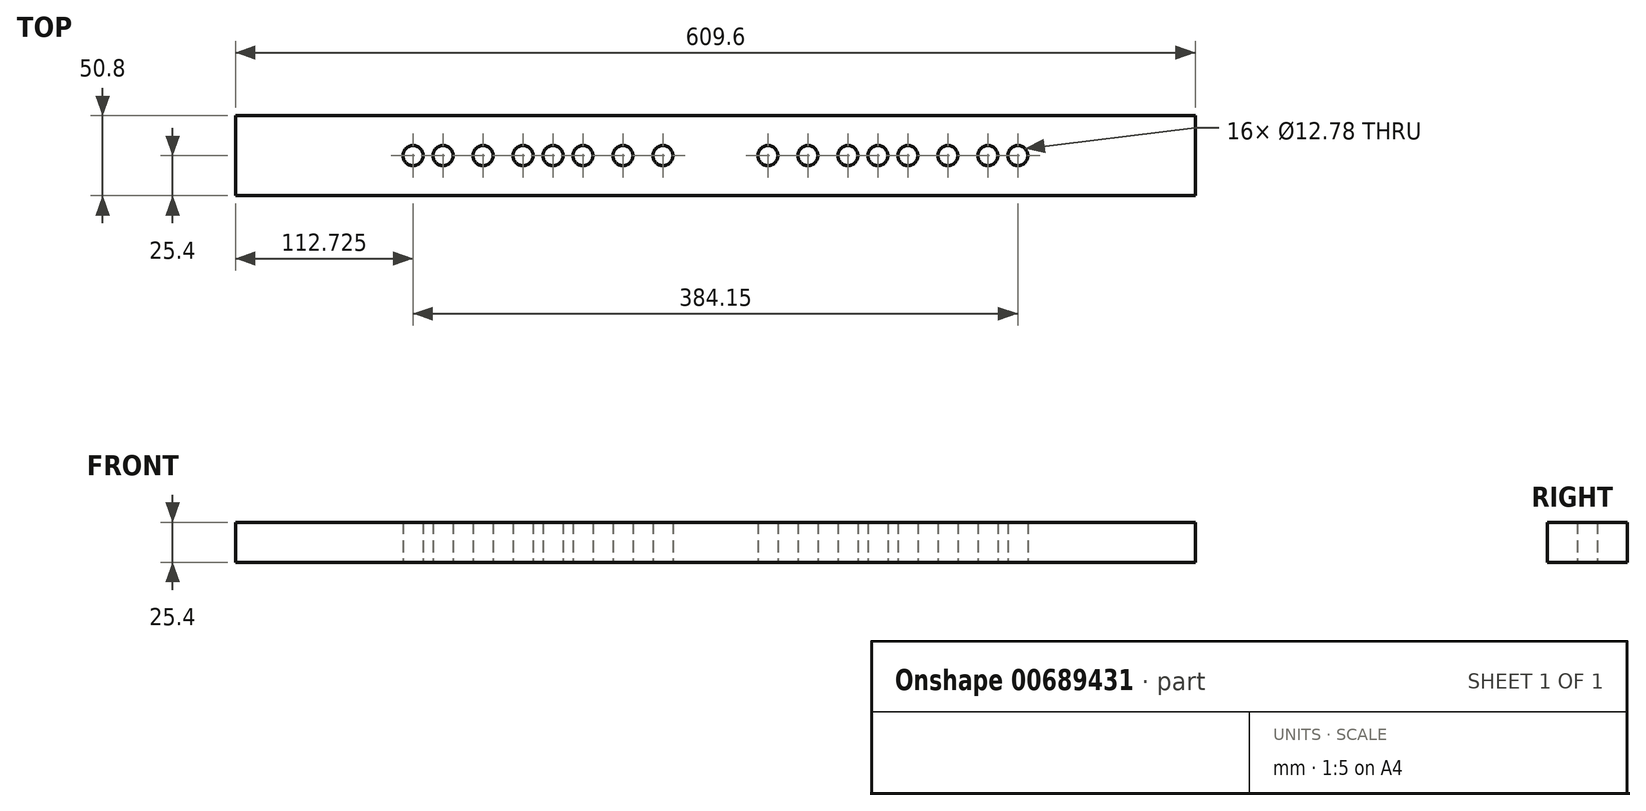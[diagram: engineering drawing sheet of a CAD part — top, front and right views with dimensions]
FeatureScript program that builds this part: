
annotation { "Feature Type Name" : "Feature", "Feature Type Description" : "" }
export const myFeature = defineFeature(function(context is Context, id is Id, definition is map)
    precondition{}
    {
        {
            var Q0;
            Q0=qCreatedBy(makeId("Top.planeOp"),FACE);
            var sketch = newSketch(context, id + "F0", { "sketchPlane" : qUnion([Q0])});
            skLineSegment(sketch, "E0.bottom", {"start": v(-304.8, 25.4) * mm, "end": v(304.8, 25.4) * mm});
            skLineSegment(sketch, "E0.top", {"start": v(-304.8, -25.4) * mm, "end": v(304.8, -25.4) * mm});
            skLineSegment(sketch, "E0.left", {"start": v(-304.8, 25.4) * mm, "end": v(-304.8, -25.4) * mm});
            skLineSegment(sketch, "E0.right", {"start": v(304.8, 25.4) * mm, "end": v(304.8, -25.4) * mm});
            skPoint(sketch, "E0.middle", {"position": v(0, 0) * mm});
            skCircle(sketch, "E1", {"center": v(-33.34, 0) * mm, "radius": 6.39 * mm});
            skCircle(sketch, "E2", {"center": v(-58.74, 0) * mm, "radius": 6.39 * mm});
            skCircle(sketch, "E3", {"center": v(-84.14, 0) * mm, "radius": 6.39 * mm});
            skCircle(sketch, "E4", {"center": v(-103.17, 0) * mm, "radius": 6.39 * mm});
            skCircle(sketch, "E5", {"center": v(-122.22, 0) * mm, "radius": 6.39 * mm});
            skCircle(sketch, "E6", {"center": v(-147.62, 0) * mm, "radius": 6.39 * mm});
            skCircle(sketch, "E7", {"center": v(-173.02, 0) * mm, "radius": 6.39 * mm});
            skCircle(sketch, "E8", {"center": v(-192.07, 0) * mm, "radius": 6.39 * mm});
            skCircle(sketch, "E9", {"center": v(33.34, 0) * mm, "radius": 6.39 * mm});
            skCircle(sketch, "E10", {"center": v(58.74, 0) * mm, "radius": 6.39 * mm});
            skCircle(sketch, "E11", {"center": v(84.14, 0) * mm, "radius": 6.39 * mm});
            skCircle(sketch, "E12", {"center": v(103.17, 0) * mm, "radius": 6.39 * mm});
            skCircle(sketch, "E13", {"center": v(122.22, 0) * mm, "radius": 6.39 * mm});
            skCircle(sketch, "E14", {"center": v(147.62, 0) * mm, "radius": 6.39 * mm});
            skCircle(sketch, "E15", {"center": v(173.02, 0) * mm, "radius": 6.39 * mm});
            skCircle(sketch, "E16", {"center": v(192.07, 0) * mm, "radius": 6.39 * mm});
            skSolve(sketch);
        }
        {
            var Q0;
            Q0=makeQuery(id+"F0.imprint","IMPRINT",FACE,{"disambiguationData":[TD([[makeQuery(id+"F0.imprint","IMPRINT",EDGE,{"derivedFrom":sQuery(id+"F0.wireOp",EDGE,"E0.bottom")}),-1.0]])]});
            extrude(context, id + "F1", {"entities" : qUnion([Q0]), "depth" : 25.4 * mm, "offsetDistance" : 25.4 * mm});
        }
    });
